# Revit family: for update_48112SGP_new
name_source: partatom
category: Plumbing Fixtures
revit_build: Autodesk Revit 2018 (Build: 20170223_1515(x64)
units: mm (PartAtom-declared; Revit-internal decimal feet)

## family parameters
Always vertical = No
Cut with Voids When Loaded = No
OmniClass Number = 23.31.11.00
OmniClass Title = Faucets
Part Type = Normal
Room Calculation Point = No
Round Connector Dimension = Use Diameter
Shared = No
Work Plane-Based = Yes

## types (2) — shared parameters
Always visible = Yes
BIMobject category = Taps & Mixers
Date of publishing = 9/28/2022 12:00:00 AM
Default Elevation = 1219.2 mm  [stored 4 ft]
Description = AXOR One Basin mixer for concealed installation wall-mounted Select with spout 220 mm 2 ticks
EAN code = 4059625469675
Edition number = 1
IFC Classification = Valve
Manufacturer = AXOR
Manufacturer name = AXOR
Masterformat 2014 Code = 22 41 39
Masterformat 2014 Description = Residential Faucets, Supplies, and Trim
Model = 48112SGP
OmniClass Code = 23-31 11 00
OmniClass Description = Faucets
Product Guid = d268bdbe-ceac-44fb-8975-aacf6f1e3ba2
Product SKU = 48112SGP
Product data url = https://bimobject.com
Product family = AXOR One
Product group = Basin mixers
Product name = 48112SGP AXOR One Basin mixer for concealed installation wall-mounted Select with spout 220 mm 2 ticks
Product url = https://www.axor-design.com
QR code = https://bimobject.com
UNSPSC Code = 301815
URL = https://www.axor-design.com
Uniclass 2015 Code = Pr_40_20_87
Uniclass 2015 Name = Taps and water supply outlet fittings
Uniformat II Code = D2010
Uniformat II Description = Plumbing Fixtures
Weight Net (Kg) = 1.5

## per-type parameters (varying)
| type | Material 1 |
| 009 Chrome | AXOR - Metal - 009 Chrome |
| 709 Matte White | AXOR - Metal - 709 Matte White |

note: [stored X ft] marks values corroborated as IEEE doubles in the binary element streams (Revit-internal decimal feet)

## geometry (parser evidence)
native form markers: Sweep x3
no freeform markers — native parametric forms only
